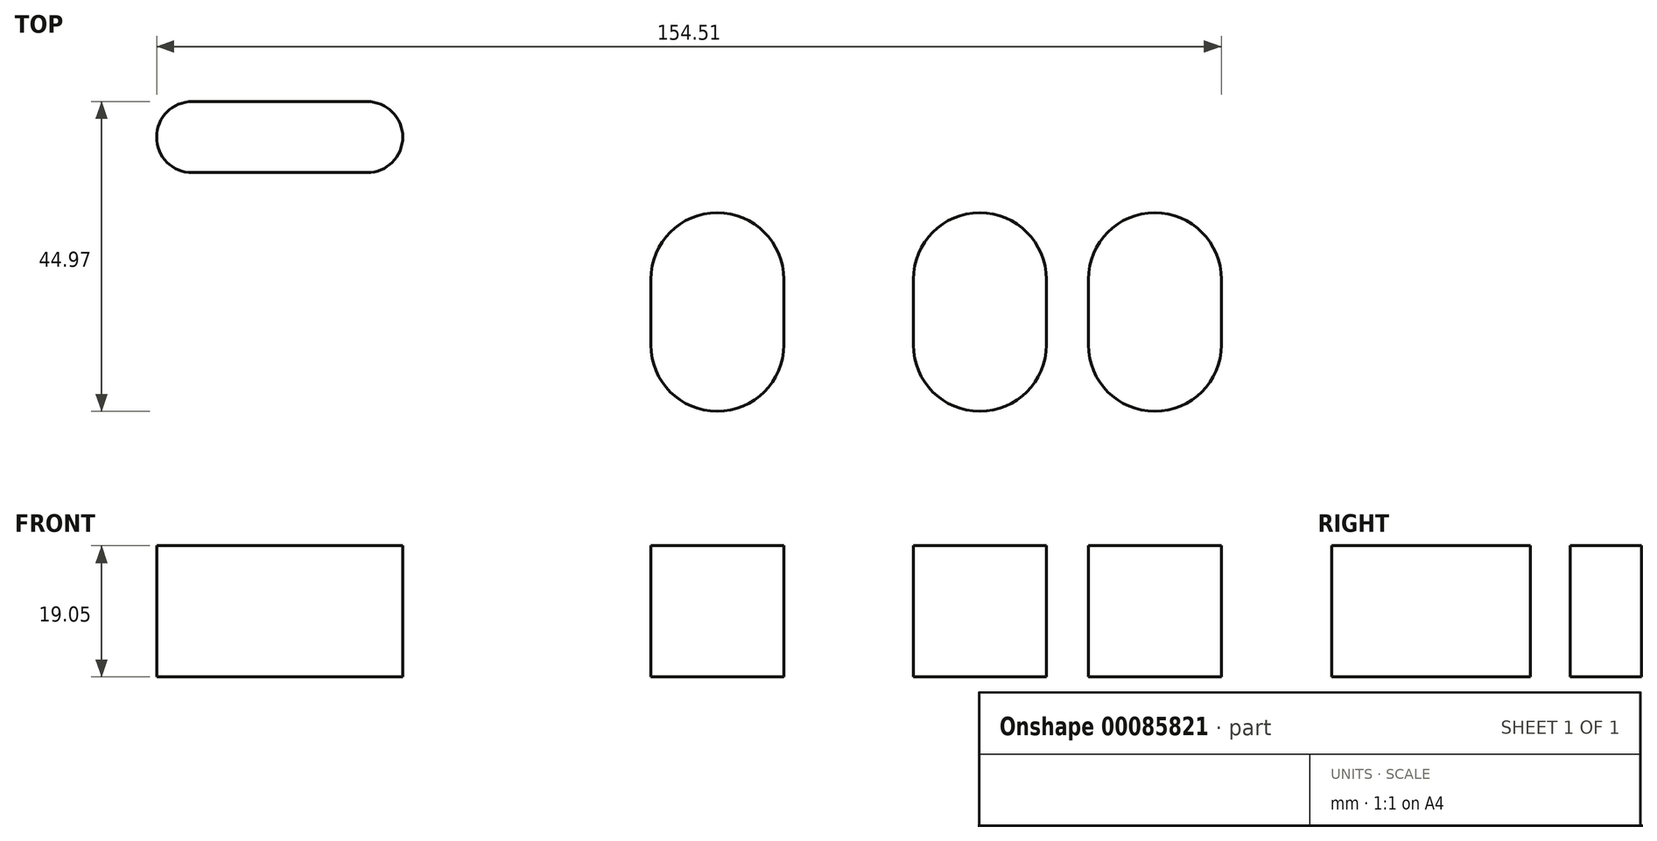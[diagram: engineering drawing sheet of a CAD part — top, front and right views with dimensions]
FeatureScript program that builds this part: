
annotation { "Feature Type Name" : "Feature", "Feature Type Description" : "" }
export const myFeature = defineFeature(function(context is Context, id is Id, definition is map)
    precondition{}
    {
        {
            var Q0;
            Q0=qCreatedBy(makeId("Top.planeOp"),FACE);
            var sketch = newSketch(context, id + "F0", { "sketchPlane" : qUnion([Q0])});
            skLineSegment(sketch, "E0.bottom", {"start": v(82.26, -47.85) * mm, "end": v(-120.94, -47.85) * mm});
            skLineSegment(sketch, "E0.top", {"start": v(82.26, 53.75) * mm, "end": v(-120.94, 53.75) * mm});
            skLineSegment(sketch, "E0.left", {"start": v(82.26, -47.85) * mm, "end": v(82.26, 53.75) * mm});
            skLineSegment(sketch, "E0.right", {"start": v(-120.94, -47.85) * mm, "end": v(-120.94, 53.75) * mm});
            skSolve(sketch);
        }
        {
            var Q0;
            Q0=makeQuery(id+"F0.imprint","IMPRINT",FACE,{"disambiguationData":[TD([[makeQuery(id+"F0.imprint","IMPRINT",EDGE,{"derivedFrom":sQuery(id+"F0.wireOp",EDGE,"E0.bottom")}),-1.0]])]});
            extrude(context, id + "F1", {"entities" : qUnion([Q0]), "depth" : 19.05 * mm, "offsetDistance" : 25.4 * mm});
        }
        {
            var Q0;
            Q0=makeQuery(id+"F1.opExtrude","CAP_FACE",FACE,{"disambiguationData":[OSD([sQuery(id+"F0.wireOp",EDGE,"E0.bottom"),sQuery(id+"F0.wireOp",EDGE,"E0.top"),sQuery(id+"F0.wireOp",EDGE,"E0.left"),sQuery(id+"F0.wireOp",EDGE,"E0.right")])],"isStart":false});
            var sketch = newSketch(context, id + "F2", { "sketchPlane" : qUnion([Q0])});
            skLineSegment(sketch, "E1", {"start": v(-19.34, 53.75) * mm, "end": v(-19.34, -47.85) * mm});
            skLineSegment(sketch, "E2", {"start": v(82.26, 2.95) * mm, "end": v(-120.94, 2.95) * mm});
            skLineSegment(sketch, "E3", {"start": v(-95.54, 28.35) * mm, "end": v(-70.14, 28.35) * mm});
            skArc(sketch, "E4.0.startCap", {"start": v(-95.54, 23.2) * mm, "mid": v(-100.7, 28.35) * mm, "end": v(-95.54, 33.5) * mm});
            skArc(sketch, "E4.0.endCap", {"start": v(-70.14, 33.5) * mm, "mid": v(-64.98, 28.35) * mm, "end": v(-70.14, 23.2) * mm});
            skLineSegment(sketch, "E4.0.left", {"start": v(-95.54, 33.5) * mm, "end": v(-70.14, 33.5) * mm});
            skLineSegment(sketch, "E4.0.right", {"start": v(-95.54, 23.2) * mm, "end": v(-70.14, 23.2) * mm});
            skArc(sketch, "E5.MirrorCS", {"start": v(31.46, 33.5) * mm, "mid": v(26.3, 28.35) * mm, "end": v(31.46, 23.2) * mm});
            skLineSegment(sketch, "E6.MirrorCS", {"start": v(56.86, 33.5) * mm, "end": v(31.46, 33.5) * mm});
            skArc(sketch, "E7.MirrorCS", {"start": v(56.86, 23.2) * mm, "mid": v(62.02, 28.35) * mm, "end": v(56.86, 33.5) * mm});
            skLineSegment(sketch, "E8.MirrorCS", {"start": v(56.86, 23.2) * mm, "end": v(31.46, 23.2) * mm});
            skArc(sketch, "E9.MirrorCS", {"start": v(-95.54, -17.3) * mm, "mid": v(-100.7, -22.45) * mm, "end": v(-95.54, -27.6) * mm});
            skLineSegment(sketch, "E10.MirrorCS", {"start": v(-95.54, -27.6) * mm, "end": v(-70.14, -27.6) * mm});
            skArc(sketch, "E11.MirrorCS", {"start": v(-70.14, -27.6) * mm, "mid": v(-64.98, -22.45) * mm, "end": v(-70.14, -17.3) * mm});
            skLineSegment(sketch, "E12.MirrorCS", {"start": v(-95.54, -17.3) * mm, "end": v(-70.14, -17.3) * mm});
            skLineSegment(sketch, "E13.MirrorCS", {"start": v(56.86, -27.6) * mm, "end": v(31.46, -27.6) * mm});
            skArc(sketch, "E14.MirrorCS", {"start": v(56.86, -17.3) * mm, "mid": v(62.02, -22.45) * mm, "end": v(56.86, -27.6) * mm});
            skLineSegment(sketch, "E15.MirrorCS", {"start": v(56.86, -17.3) * mm, "end": v(31.46, -17.3) * mm});
            skArc(sketch, "E16.MirrorCS", {"start": v(31.46, -27.6) * mm, "mid": v(26.3, -22.45) * mm, "end": v(31.46, -17.3) * mm});
            skArc(sketch, "E17.0.startCap", {"start": v(-95.54, 20.41) * mm, "mid": v(-103.48, 28.35) * mm, "end": v(-95.54, 36.29) * mm});
            skArc(sketch, "E17.0.endCap", {"start": v(-70.14, 36.29) * mm, "mid": v(-62.2, 28.35) * mm, "end": v(-70.14, 20.41) * mm});
            skLineSegment(sketch, "E17.0.left", {"start": v(-95.54, 36.29) * mm, "end": v(-70.14, 36.29) * mm});
            skLineSegment(sketch, "E17.0.right", {"start": v(-95.54, 20.41) * mm, "end": v(-70.14, 20.41) * mm});
            skArc(sketch, "E18.MirrorCS", {"start": v(31.46, 36.29) * mm, "mid": v(23.52, 28.35) * mm, "end": v(31.46, 20.41) * mm});
            skLineSegment(sketch, "E19.MirrorCS", {"start": v(56.86, 36.29) * mm, "end": v(31.46, 36.29) * mm});
            skArc(sketch, "E20.MirrorCS", {"start": v(56.86, 20.41) * mm, "mid": v(64.8, 28.35) * mm, "end": v(56.86, 36.29) * mm});
            skLineSegment(sketch, "E21.MirrorCS", {"start": v(56.86, 20.41) * mm, "end": v(31.46, 20.41) * mm});
            skArc(sketch, "E22.MirrorCS", {"start": v(-70.14, -30.39) * mm, "mid": v(-62.2, -22.45) * mm, "end": v(-70.14, -14.51) * mm});
            skLineSegment(sketch, "E23.MirrorCS", {"start": v(-95.54, -30.39) * mm, "end": v(-70.14, -30.39) * mm});
            skArc(sketch, "E24.MirrorCS", {"start": v(-95.54, -14.51) * mm, "mid": v(-103.48, -22.45) * mm, "end": v(-95.54, -30.39) * mm});
            skLineSegment(sketch, "E25.MirrorCS", {"start": v(-95.54, -14.51) * mm, "end": v(-70.14, -14.51) * mm});
            skLineSegment(sketch, "E26.MirrorCS", {"start": v(56.86, -30.39) * mm, "end": v(31.46, -30.39) * mm});
            skArc(sketch, "E27.MirrorCS", {"start": v(31.46, -30.39) * mm, "mid": v(23.52, -22.45) * mm, "end": v(31.46, -14.51) * mm});
            skArc(sketch, "E28.MirrorCS", {"start": v(56.86, -14.51) * mm, "mid": v(64.8, -22.45) * mm, "end": v(56.86, -30.39) * mm});
            skLineSegment(sketch, "E29.MirrorCS", {"start": v(56.86, -14.51) * mm, "end": v(31.46, -14.51) * mm});
            skSolve(sketch);
        }
        {
            var Q0;
            Q0=makeQuery(id+"F2.imprint","IMPRINT",FACE,{"disambiguationData":[TD([[makeQuery(id+"F2.imprint","IMPRINT",EDGE,{"derivedFrom":sQuery(id+"F2.wireOp",EDGE,"E4.0.startCap")}),-1.0]])]});
            var Q1;
            Q1=makeQuery(id+"F2.imprint","IMPRINT",FACE,{"disambiguationData":[TD([[makeQuery(id+"F2.imprint","IMPRINT",EDGE,{"derivedFrom":sQuery(id+"F2.wireOp",EDGE,"E5.MirrorCS")}),1.0]])]});
            var Q2;
            Q2=makeQuery(id+"F2.imprint","IMPRINT",FACE,{"disambiguationData":[TD([[makeQuery(id+"F2.imprint","IMPRINT",EDGE,{"derivedFrom":sQuery(id+"F2.wireOp",EDGE,"E13.MirrorCS")}),-1.0]])]});
            var Q3;
            Q3=makeQuery(id+"F2.imprint","IMPRINT",FACE,{"disambiguationData":[TD([[makeQuery(id+"F2.imprint","IMPRINT",EDGE,{"derivedFrom":sQuery(id+"F2.wireOp",EDGE,"E9.MirrorCS")}),1.0]])]});
            extrude(context, id + "F3", {"entities" : qUnion([Q0, Q1, Q2, Q3]), "operationType" : NewBodyOperationType.REMOVE, "endBound" : BoundingType.THROUGH_ALL, "oppositeDirection" : true, "depth" : 25.4 * mm, "offsetDistance" : 25.4 * mm});
        }
        {
            var Q0;
            Q0 = qSketchRegion(id + "F2", true);
            extrude(context, id + "F4", {"entities" : qUnion([Q0]), "operationType" : NewBodyOperationType.REMOVE, "oppositeDirection" : true, "depth" : 9.52 * mm, "offsetDistance" : 25.4 * mm});
        }
        {
            var Q0;
            Q0=makeQuery(id+"F1.opExtrude","CAP_FACE",FACE,{"disambiguationData":[OSD([sQuery(id+"F0.wireOp",EDGE,"E0.bottom"),sQuery(id+"F0.wireOp",EDGE,"E0.top"),sQuery(id+"F0.wireOp",EDGE,"E0.left"),sQuery(id+"F0.wireOp",EDGE,"E0.right")])],"isStart":false});
            var sketch = newSketch(context, id + "F5", { "sketchPlane" : qUnion([Q0])});
            skPoint(sketch, "E30", {"position": v(-19.34, 2.32) * mm});
            skLineSegment(sketch, "E31", {"start": v(-120.94, 2.95) * mm, "end": v(82.26, 2.95) * mm});
            skLineSegment(sketch, "E32", {"start": v(-19.34, 2.95) * mm, "end": v(-19.34, -1.81) * mm});
            skLineSegment(sketch, "E33.MirrorCS", {"start": v(-19.34, 2.95) * mm, "end": v(-19.34, 7.71) * mm});
            skLineSegment(sketch, "E34", {"start": v(-19.34, 7.71) * mm, "end": v(-19.34, -1.81) * mm});
            skArc(sketch, "E35.0.startCap", {"start": v(-29, 7.71) * mm, "mid": v(-19.34, 17.37) * mm, "end": v(-9.69, 7.71) * mm});
            skArc(sketch, "E35.0.endCap", {"start": v(-9.69, -1.81) * mm, "mid": v(-19.34, -11.46) * mm, "end": v(-29, -1.81) * mm});
            skLineSegment(sketch, "E35.0.left", {"start": v(-9.69, 7.71) * mm, "end": v(-9.69, -1.81) * mm});
            skLineSegment(sketch, "E35.0.right", {"start": v(-29, 7.71) * mm, "end": v(-29, -1.81) * mm});
            skLineSegment(sketch, "E36.0", {"start": v(18.76, 7.71) * mm, "end": v(18.76, -1.81) * mm});
            skLineSegment(sketch, "E37.0", {"start": v(44.16, 7.71) * mm, "end": v(44.16, -1.81) * mm});
            skLineSegment(sketch, "E38.0", {"start": v(88.61, -54.2) * mm, "end": v(88.61, 60.1) * mm});
            skLineSegment(sketch, "E38.1", {"start": v(-127.29, -54.2) * mm, "end": v(88.61, -54.2) * mm});
            skLineSegment(sketch, "E38.2", {"start": v(-127.29, 60.1) * mm, "end": v(-127.29, -54.2) * mm});
            skLineSegment(sketch, "E38.3", {"start": v(88.61, 60.1) * mm, "end": v(-127.29, 60.1) * mm});
            skArc(sketch, "E39.0.startCap", {"start": v(9.1, 7.71) * mm, "mid": v(18.76, 17.37) * mm, "end": v(28.41, 7.71) * mm});
            skArc(sketch, "E39.0.endCap", {"start": v(28.41, -1.81) * mm, "mid": v(18.76, -11.46) * mm, "end": v(9.1, -1.81) * mm});
            skLineSegment(sketch, "E39.0.left", {"start": v(28.41, 7.71) * mm, "end": v(28.41, -1.81) * mm});
            skLineSegment(sketch, "E39.0.right", {"start": v(9.1, 7.71) * mm, "end": v(9.1, -1.81) * mm});
            skArc(sketch, "E39.1.startCap", {"start": v(34.5, 7.71) * mm, "mid": v(44.16, 17.37) * mm, "end": v(53.81, 7.71) * mm});
            skArc(sketch, "E39.1.endCap", {"start": v(53.81, -1.81) * mm, "mid": v(44.16, -11.46) * mm, "end": v(34.5, -1.81) * mm});
            skLineSegment(sketch, "E39.1.left", {"start": v(53.81, 7.71) * mm, "end": v(53.81, -1.81) * mm});
            skLineSegment(sketch, "E39.1.right", {"start": v(34.5, 7.71) * mm, "end": v(34.5, -1.81) * mm});
            skSolve(sketch);
        }
        {
            var Q0;
            {var subQ0=sQuery(id+"F5.wireOp",EDGE,"E35.0.startCap");Q0=makeQuery(id+"F5.imprint","IMPRINT",FACE,{"disambiguationData":[TD([[makeQuery(id+"F5.imprint","IMPRINT",EDGE,{"derivedFrom":subQ0}),-1.0]])]});}
            var Q1;
            {var subQ1=sQuery(id+"F5.wireOp",EDGE,"E35.0.endCap");Q1=makeQuery(id+"F5.imprint","IMPRINT",FACE,{"disambiguationData":[TD([[makeQuery(id+"F5.imprint","IMPRINT",EDGE,{"derivedFrom":subQ1}),-1.0]])]});}
            var Q2;
            {var subQ1=sQuery(id+"F5.wireOp",EDGE,"E39.0.startCap");Q2=makeQuery(id+"F5.imprint","IMPRINT",FACE,{"disambiguationData":[TD([[makeQuery(id+"F5.imprint","IMPRINT",EDGE,{"derivedFrom":subQ1}),-1.0]])]});}
            var Q3;
            {var subQ1=sQuery(id+"F5.wireOp",EDGE,"E39.0.endCap");Q3=makeQuery(id+"F5.imprint","IMPRINT",FACE,{"disambiguationData":[TD([[makeQuery(id+"F5.imprint","IMPRINT",EDGE,{"derivedFrom":subQ1}),-1.0]])]});}
            var Q4;
            {var subQ0=sQuery(id+"F5.wireOp",EDGE,"E39.1.startCap");Q4=makeQuery(id+"F5.imprint","IMPRINT",FACE,{"disambiguationData":[TD([[makeQuery(id+"F5.imprint","IMPRINT",EDGE,{"derivedFrom":subQ0}),-1.0]])]});}
            var Q5;
            {var subQ1=sQuery(id+"F5.wireOp",EDGE,"E39.1.endCap");Q5=makeQuery(id+"F5.imprint","IMPRINT",FACE,{"disambiguationData":[TD([[makeQuery(id+"F5.imprint","IMPRINT",EDGE,{"derivedFrom":subQ1}),-1.0]])]});}
            extrude(context, id + "F6", {"entities" : qUnion([Q0, Q1, Q2, Q3, Q4, Q5]), "operationType" : NewBodyOperationType.REMOVE, "endBound" : BoundingType.THROUGH_ALL, "oppositeDirection" : true, "depth" : 25.4 * mm, "offsetDistance" : 25.4 * mm});
        }
    });
